# Revit family: Hager-WITTY PRO WALL MOUNTED-fr-CH-CH
name_source: partatom
category: Electrical Fixtures
units: mm (PartAtom-declared; Revit-internal decimal feet)

## family parameters
Always vertical = Yes
Cut with Voids When Loaded = No
Host = Wall
Maintain Annotation Orientation = No
OmniClass Number = 23.75.00.00
OmniClass Title = Climate Control (HVAC)
Part Type = Normal
Room Calculation Point = No
Round Connector Dimension = Use Diameter
Shared = No

## types (2) — shared parameters
BC_METADATA = {"ObjectGuid":"b7395028-ef9e-46b8-b49f-e0fe9c8fa070","ModelGuid":"b1efb829-c177-4a88-8b0d-f632edc25d22","VariantGuid":"c7b0c534-fef0-4725-a2d6-e8a658ebdb92","Revision":"#2","VariantName":"REF 1"}
BC_MODEL_ID = 1528887
BC_OBJECT_ID = 511149
BC_OBJECT_VERSION = #1
Code hager = ADD_EC002883_ECVS_WO
EF000003 - mode de montage = montage mural
EF000008 - largeur = 250 mm  [stored 0.82021 ft]
EF000040 - hauteur = 370 mm  [stored 1.21391 ft]
EF000049 - profondeur = 150 mm  [stored 0.492126 ft]
EF000458 - avec affichage = No
EF001596 - matériau du boîtier = matière synthétique
EF002136 - puissance de raccordement nominale = 22000 W
EF003840 - tension d'entrée = 400 V
EF004293 - résistance aux chocs = IK10
EF005455 - fréquence = 50/60 Hz
EF005474 - indice de protection (IP) = IP55
EF007001 - tension de sortie DC = 0 V
EF007353 - courant de sortie max. DC = 0 A
EF009078 - nombre de points de chargement = 1
EF009089 - coffret d'abonnés = No
EF009300 - puissance max. par point de chargement = 22000 W
EF009305 - nombre de prises de chargement type 2 = 1
EF009313 - avec compteur d'énergie = Yes
EF009314 - avec disjoncteur = No
EF009547 - LTE = No
EF011072 - compatible IFTTT = No
EF012191 - avec lecteur de carte RFID intégré = Yes
EF012361 - NFC (Near Field Communication) = No
EF013154 - raccordable via Wi-Fi = Yes
EF014925 - compatible avec Apple HomeKit = No
EF014926 - compatible avec Google Assistant = No
EF014927 - compatible avec Amazon Alexa = No
EF016385 - standard de téléphonie mobile 5G = No
EF017508 - peut être mis en réseau en tant que maître = No
EF017509 - détection de courant de défaut DC = No
EF017511 - avec interrupteur à clé = No
EF017512 - exportation de l'historique de charge = Yes
EF017513 - Open Charge Point Protocol (OCPP) version = 1.6
EF017515 - Plug and charge (ISO 15118) = No
EF017517 - peut être mis en réseau en tant qu'extension = No
EF017663 - câble de recharge verrouillable en permanence sur la station de charge = No
EF017664 - peut être mis en réseau via LAN = Yes
EF017665 - avec compteur d'énergie compatible MID = Yes
EF017668 - gestion de la charge statique intégrée = No
EF017669 - convient pour la gestion dynamique de la charge = Yes
EF017672 - backend intégré = No
EF017972 - utilisation et configuration via app = Yes
EF025053 - type de raccordement côté installation = triphasé
EFDE0066 - conforme à la législation sur l'étalonnage = No
ETIM class code = EC002883
ETIM class name = Charging device E-Mobility
HG000003-Range = WITTY PRO
HG000065-With socket TE = No
HG000099-Onfly Template ID = WittyOne_EVCS_Wall_Mounted
Manufacturer = hager France
Name = WITTY PRO WALL MOUNTED-CH
Name BIM&CO = Electricity
Name hager = ADD_ChargingStation_EC002883
Reference description = ECVS Witty 1x22kW 3P T2S
zero-valued in all types: Default Elevation, EF006577 - nombre de prises CEE (IEC 60309), EF008200 - section de conducteur connectable, EF009091 - nombre d'interrupteurs différentiels type A, EF009092 - nombre d'interrupteurs différentiels type B, EF009301 - nombre de prises mobiles de charge type 1, EF009302 - nombre de prises mobiles de charge type 1 CCS, EF009303 - nombre de prises mobiles de charge type 2, EF009304 - nombre de prises mobiles de charge type 2 CCS, EF009306 - nombre de prises mobiles de charge GB AC, EF009307 - nombre de prises mobiles de charge GB DC, EF009308 - nombre de prises de chargement GB, EF009309 - nombre de prises de chargement type 3, EF009310 - nombre de prises mobiles de charge CHAdeMO, EF009311 - nombre de prises domestiques

## per-type parameters (varying)
| type | BC_VARIANT_ID | EF014895 - longueur du câble de charge | HG000004-Manufacturer reference |
| WITTY PRO-1x22kW-3P-XVL122SCH-WALL MOUNTED | 1164666 | 0 mm  [stored 0 ft] | XVL122SCH |
| WITTY PRO-1x22kW-3P-XVL122CCH-WALL MOUNTED | 1164667 | 6500 mm  [stored 21.3255 ft] | XVL122CCH |

note: column(s) folded — value = type name in every type: Reference

note: [stored X ft] marks values corroborated as IEEE doubles in the binary element streams (Revit-internal decimal feet)
